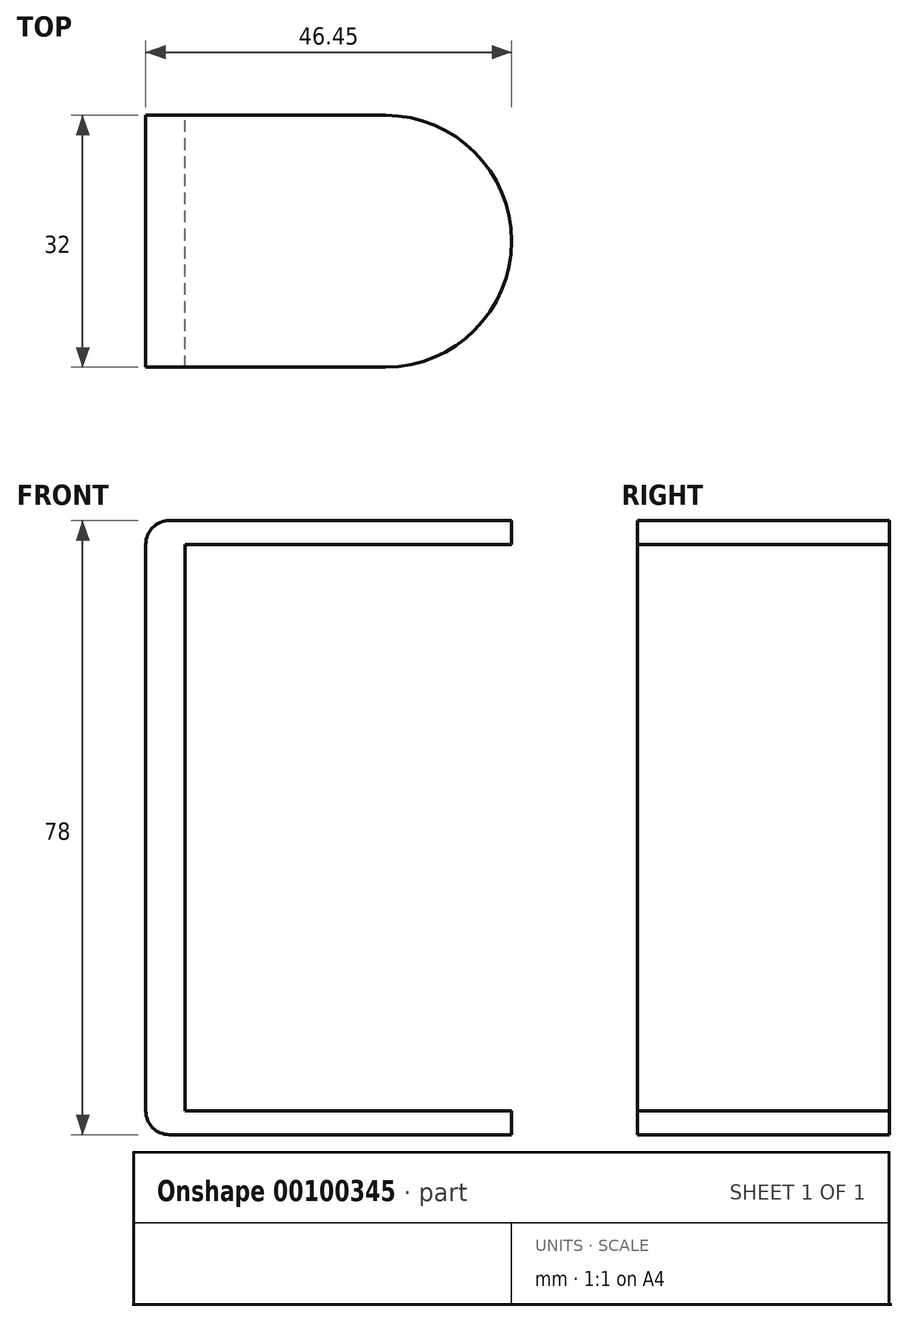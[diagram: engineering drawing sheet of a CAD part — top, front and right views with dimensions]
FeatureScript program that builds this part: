
annotation { "Feature Type Name" : "Feature", "Feature Type Description" : "" }
export const myFeature = defineFeature(function(context is Context, id is Id, definition is map)
    precondition{}
    {
        {
            var Q0;
            Q0=qCreatedBy(makeId("Front.planeOp"),FACE);
            var sketch = newSketch(context, id + "F0", { "sketchPlane" : qUnion([Q0])});
            skLineSegment(sketch, "E0.bottom", {"start": v(48, -24) * mm, "end": v(0, -24) * mm});
            skLineSegment(sketch, "E0.top", {"start": v(48, 24) * mm, "end": v(0, 24) * mm});
            skLineSegment(sketch, "E0.left", {"start": v(48, -24) * mm, "end": v(48, 24) * mm});
            skLineSegment(sketch, "E0.right", {"start": v(0, -24) * mm, "end": v(0, 24) * mm});
            skPoint(sketch, "E0.middle", {"position": v(24, 0) * mm});
            skLineSegment(sketch, "E1.bottom", {"start": v(-11.46, -18) * mm, "end": v(-47.46, -18) * mm});
            skLineSegment(sketch, "E1.top", {"start": v(-11.46, 18) * mm, "end": v(-47.46, 18) * mm});
            skLineSegment(sketch, "E1.left", {"start": v(-11.46, -18) * mm, "end": v(-11.46, 18) * mm});
            skLineSegment(sketch, "E1.right", {"start": v(-47.46, -18) * mm, "end": v(-47.46, 18) * mm});
            skPoint(sketch, "E1.middle", {"position": v(-29.46, 0) * mm});
            skLineSegment(sketch, "E2.bottom", {"start": v(-11.46, -54) * mm, "end": v(-47.46, -54) * mm});
            skLineSegment(sketch, "E2.left", {"start": v(-11.46, -54) * mm, "end": v(-11.46, -18) * mm});
            skLineSegment(sketch, "E2.right", {"start": v(-47.46, -54) * mm, "end": v(-47.46, -18) * mm});
            skPoint(sketch, "E2.middle", {"position": v(-29.46, -36) * mm});
            skLineSegment(sketch, "E3", {"start": v(-29.46, 0) * mm, "end": v(-29.46, -36) * mm, "construction": true});
            skLineSegment(sketch, "E4", {"start": v(-29.46, 0) * mm, "end": v(24, 0) * mm, "construction": true});
            skCircle(sketch, "E5", {"center": v(-29.46, 0) * mm, "radius": 25.46 * mm, "construction": true});
            skLineSegment(sketch, "E6", {"start": v(-51.65, -21) * mm, "end": v(-8.4, -21) * mm, "construction": true});
            skLineSegment(sketch, "E7.0", {"start": v(-41.46, -48) * mm, "end": v(-41.46, -24) * mm, "construction": true});
            skLineSegment(sketch, "E7.1", {"start": v(-17.46, -48) * mm, "end": v(-41.46, -48) * mm, "construction": true});
            skLineSegment(sketch, "E7.2", {"start": v(-17.46, -48) * mm, "end": v(-17.46, -24) * mm, "construction": true});
            skLineSegment(sketch, "E7.3", {"start": v(-17.46, -24) * mm, "end": v(-41.46, -24) * mm, "construction": true});
            skLineSegment(sketch, "E8.0", {"start": v(-17.46, 12) * mm, "end": v(-41.46, 12) * mm, "construction": true});
            skLineSegment(sketch, "E8.1", {"start": v(-17.46, -12) * mm, "end": v(-17.46, 12) * mm, "construction": true});
            skLineSegment(sketch, "E8.2", {"start": v(-17.46, -12) * mm, "end": v(-41.46, -12) * mm, "construction": true});
            skLineSegment(sketch, "E8.3", {"start": v(-41.46, -12) * mm, "end": v(-41.46, 12) * mm, "construction": true});
            skLineSegment(sketch, "E9.0", {"start": v(42, 18) * mm, "end": v(6, 18) * mm, "construction": true});
            skLineSegment(sketch, "E9.1", {"start": v(42, -18) * mm, "end": v(42, 18) * mm, "construction": true});
            skLineSegment(sketch, "E9.2", {"start": v(42, -18) * mm, "end": v(6, -18) * mm, "construction": true});
            skLineSegment(sketch, "E9.3", {"start": v(6, -18) * mm, "end": v(6, 18) * mm, "construction": true});
            skLineSegment(sketch, "E10", {"start": v(-11.46, 18) * mm, "end": v(-4, 18) * mm, "construction": true});
            skLineSegment(sketch, "E11", {"start": v(-4, 18) * mm, "end": v(-4, -18) * mm, "construction": true});
            skLineSegment(sketch, "E12", {"start": v(-4, -18) * mm, "end": v(-11.46, -18) * mm, "construction": true});
            skLineSegment(sketch, "E13.bottom", {"start": v(-29.46, 25.46) * mm, "end": v(-4, 0) * mm, "construction": true});
            skLineSegment(sketch, "E13.top", {"start": v(-80.37, -25.46) * mm, "end": v(-54.91, -50.91) * mm, "construction": true});
            skLineSegment(sketch, "E13.left", {"start": v(-29.46, 25.46) * mm, "end": v(-80.37, -25.46) * mm, "construction": true});
            skLineSegment(sketch, "E13.right", {"start": v(-4, 0) * mm, "end": v(-54.91, -50.91) * mm, "construction": true});
            skLineSegment(sketch, "E14", {"start": v(-29.46, 25.46) * mm, "end": v(-29.46, -25.46) * mm, "construction": true});
            skSolve(sketch);
        }
        {
            var Q0;
            Q0=qCreatedBy(makeId("Front.planeOp"),FACE);
            var sketch = newSketch(context, id + "F1", { "sketchPlane" : qUnion([Q0])});
            skCircle(sketch, "E15", {"center": v(-29.46, 0) * mm, "radius": 16 * mm});
            skLineSegment(sketch, "E16", {"start": v(0, 22) * mm, "end": v(-3, 22) * mm});
            skLineSegment(sketch, "E17", {"start": v(-3, 22) * mm, "end": v(-32.8, 15.65) * mm});
            skLineSegment(sketch, "E18", {"start": v(0, 22) * mm, "end": v(0, -22) * mm});
            skLineSegment(sketch, "E19", {"start": v(0, -22) * mm, "end": v(-3, -22) * mm});
            skLineSegment(sketch, "E20", {"start": v(-3, -22) * mm, "end": v(-32.8, -15.65) * mm});
            skLineSegment(sketch, "E21", {"start": v(-3, 22) * mm, "end": v(-3, -22) * mm, "construction": true});
            skSolve(sketch);
        }
        {
            var Q0;
            Q0 = qSketchRegion(id + "F1", true);
            extrude(context, id + "F2", {"entities" : qUnion([Q0]), "depth" : (48 / 2 - 2) * mm});
        }
        {
            var Q0;
            Q0=qCreatedBy(makeId("Top.planeOp"),FACE);
            var sketch = newSketch(context, id + "F3", { "sketchPlane" : qUnion([Q0])});
            skLineSegment(sketch, "E22.bottom", {"start": v(-4, 0) * mm, "end": v(-47.46, 0) * mm});
            skLineSegment(sketch, "E22.top", {"start": v(-4, -18) * mm, "end": v(-47.46, -18) * mm});
            skLineSegment(sketch, "E22.left", {"start": v(-4, 0) * mm, "end": v(-4, -18) * mm});
            skLineSegment(sketch, "E22.right", {"start": v(-47.46, 0) * mm, "end": v(-47.46, -18) * mm});
            skLineSegment(sketch, "E23", {"start": v(-47.46, -21) * mm, "end": v(-13.46, -21) * mm});
            skLineSegment(sketch, "E24", {"start": v(-13.46, -21) * mm, "end": v(0, -22) * mm});
            skLineSegment(sketch, "E25", {"start": v(0, -22) * mm, "end": v(-47.46, -22) * mm});
            skLineSegment(sketch, "E26", {"start": v(-47.46, -22) * mm, "end": v(-47.46, -21) * mm});
            skLineSegment(sketch, "E27", {"start": v(-13.46, -21) * mm, "end": v(-13.46, 0) * mm, "construction": true});
            skSolve(sketch);
        }
        {
            var Q0;
            Q0 = qSketchRegion(id + "F3", true);
            extrude(context, id + "F4", {"entities" : qUnion([Q0]), "operationType" : NewBodyOperationType.REMOVE, "endBound" : BoundingType.THROUGH_ALL, "oppositeDirection" : true, "depth" : 25 * mm, "hasSecondDirection" : true, "secondDirectionOppositeDirection" : false, "secondDirectionDepth" : 25 * mm});
        }
        {
            var Q0;
            Q0=makeQuery(id+"F4.boolean.opBoolean","COPY",EDGE,{"derivedFrom":makeQuery(id+"F4.opExtrude","SWEPT_EDGE",EDGE,{"disambiguationData":[OSD([sQuery(id+"F3.wireOp",EDGE,"E22.top"),sQuery(id+"F3.wireOp",EDGE,"E22.left")])]})});
            fillet(context, id + "F5", {"entities" : qUnion([Q0]), "radius" : 5 * mm, "tangentPropagation" : true, "allowEdgeOverflow" : false});
        }
        {
            var Q0;
            Q0=qCreatedBy(makeId("Front.planeOp"),FACE);
            var sketch = newSketch(context, id + "F6", { "sketchPlane" : qUnion([Q0])});
            skLineSegment(sketch, "E28", {"start": v(-13.46, 18) * mm, "end": v(-54.91, 18) * mm});
            skLineSegment(sketch, "E29", {"start": v(-54.91, 18) * mm, "end": v(-54.91, -54) * mm});
            skLineSegment(sketch, "E30", {"start": v(-54.91, -54) * mm, "end": v(-13.46, -54) * mm});
            skLineSegment(sketch, "E31", {"start": v(-13.46, -54) * mm, "end": v(-13.46, -57) * mm});
            skLineSegment(sketch, "E32", {"start": v(-13.46, -57) * mm, "end": v(-56.91, -57) * mm});
            skLineSegment(sketch, "E33", {"start": v(-59.91, -54) * mm, "end": v(-59.91, 18) * mm});
            skLineSegment(sketch, "E34", {"start": v(-56.91, 21) * mm, "end": v(-13.46, 21) * mm});
            skLineSegment(sketch, "E35", {"start": v(-13.46, 21) * mm, "end": v(-13.46, 18) * mm});
            skPoint(sketch, "E36.visualSharp", {"position": v(-59.91, 21) * mm});
            skArc(sketch, "E36.filletArc", {"start": v(-56.91, 21) * mm, "mid": v(-59.03, 20.12) * mm, "end": v(-59.91, 18) * mm});
            skPoint(sketch, "E37.visualSharp", {"position": v(-59.91, -57) * mm});
            skArc(sketch, "E37.filletArc", {"start": v(-59.91, -54) * mm, "mid": v(-59.03, -56.12) * mm, "end": v(-56.91, -57) * mm});
            skSolve(sketch);
        }
        {
            var Q0;
            Q0=makeQuery(id+"F6.imprint","IMPRINT",FACE,{"disambiguationData":[TD([[makeQuery(id+"F6.imprint","IMPRINT",EDGE,{"derivedFrom":sQuery(id+"F6.wireOp",EDGE,"E28")}),-1.0]])]});
            extrude(context, id + "F7", {"entities" : qUnion([Q0]), "depth" : (36 / 2 - 2) * mm});
        }
        {
            var Q0;
            Q0=qCreatedBy(makeId("Top.planeOp"),FACE);
            var sketch = newSketch(context, id + "F8", { "sketchPlane" : qUnion([Q0])});
            skCircle(sketch, "E38", {"center": v(-29.46, 0) * mm, "radius": 16 * mm});
            skLineSegment(sketch, "E39", {"start": v(-29.46, -16) * mm, "end": v(-59.91, -16) * mm});
            skLineSegment(sketch, "E40", {"start": v(-59.91, -16) * mm, "end": v(-59.91, 0) * mm});
            skLineSegment(sketch, "E41", {"start": v(-59.91, 0) * mm, "end": v(-45.46, 0) * mm});
            skSolve(sketch);
        }
        {
            var Q0;
            Q0 = qSketchRegion(id + "F8", true);
            extrude(context, id + "F9", {"entities" : qUnion([Q0]), "operationType" : NewBodyOperationType.INTERSECT, "endBound" : BoundingType.THROUGH_ALL, "depth" : 25 * mm, "hasSecondDirection" : true, "secondDirectionBound" : SecondDirectionBoundingType.THROUGH_ALL, "secondDirectionOppositeDirection" : true, "secondDirectionDepth" : 25 * mm});
        }
        {
            var Q0;
            Q0=makeQuery(id+"F2.opExtrude","SWEPT_BODY",BODY,{"disambiguationData":[OSD([sQuery(id+"F1.wireOp",EDGE,"E15"),sQuery(id+"F1.wireOp",EDGE,"E16"),sQuery(id+"F1.wireOp",EDGE,"E17"),sQuery(id+"F1.wireOp",EDGE,"E18"),sQuery(id+"F1.wireOp",EDGE,"E19"),sQuery(id+"F1.wireOp",EDGE,"E20")])]});
            var Q1;
            Q1=makeQuery(id+"F7.opExtrude","SWEPT_BODY",BODY,{"disambiguationData":[OSD([sQuery(id+"F6.wireOp",EDGE,"E28"),sQuery(id+"F6.wireOp",EDGE,"E29"),sQuery(id+"F6.wireOp",EDGE,"E30"),sQuery(id+"F6.wireOp",EDGE,"E31"),sQuery(id+"F6.wireOp",EDGE,"E32"),sQuery(id+"F6.wireOp",EDGE,"E33"),sQuery(id+"F6.wireOp",EDGE,"E34"),sQuery(id+"F6.wireOp",EDGE,"E35"),sQuery(id+"F6.wireOp",EDGE,"E36.filletArc"),sQuery(id+"F6.wireOp",EDGE,"E37.filletArc")])]});
            var Q2;
            Q2=qCreatedBy(makeId("Front.planeOp"),FACE);
            mirror(context, id + "F10", {"operationType" : NewBodyOperationType.ADD, "entities" : qUnion([Q0, Q1]), "mirrorPlane" : qUnion([Q2])});
        }
    });
